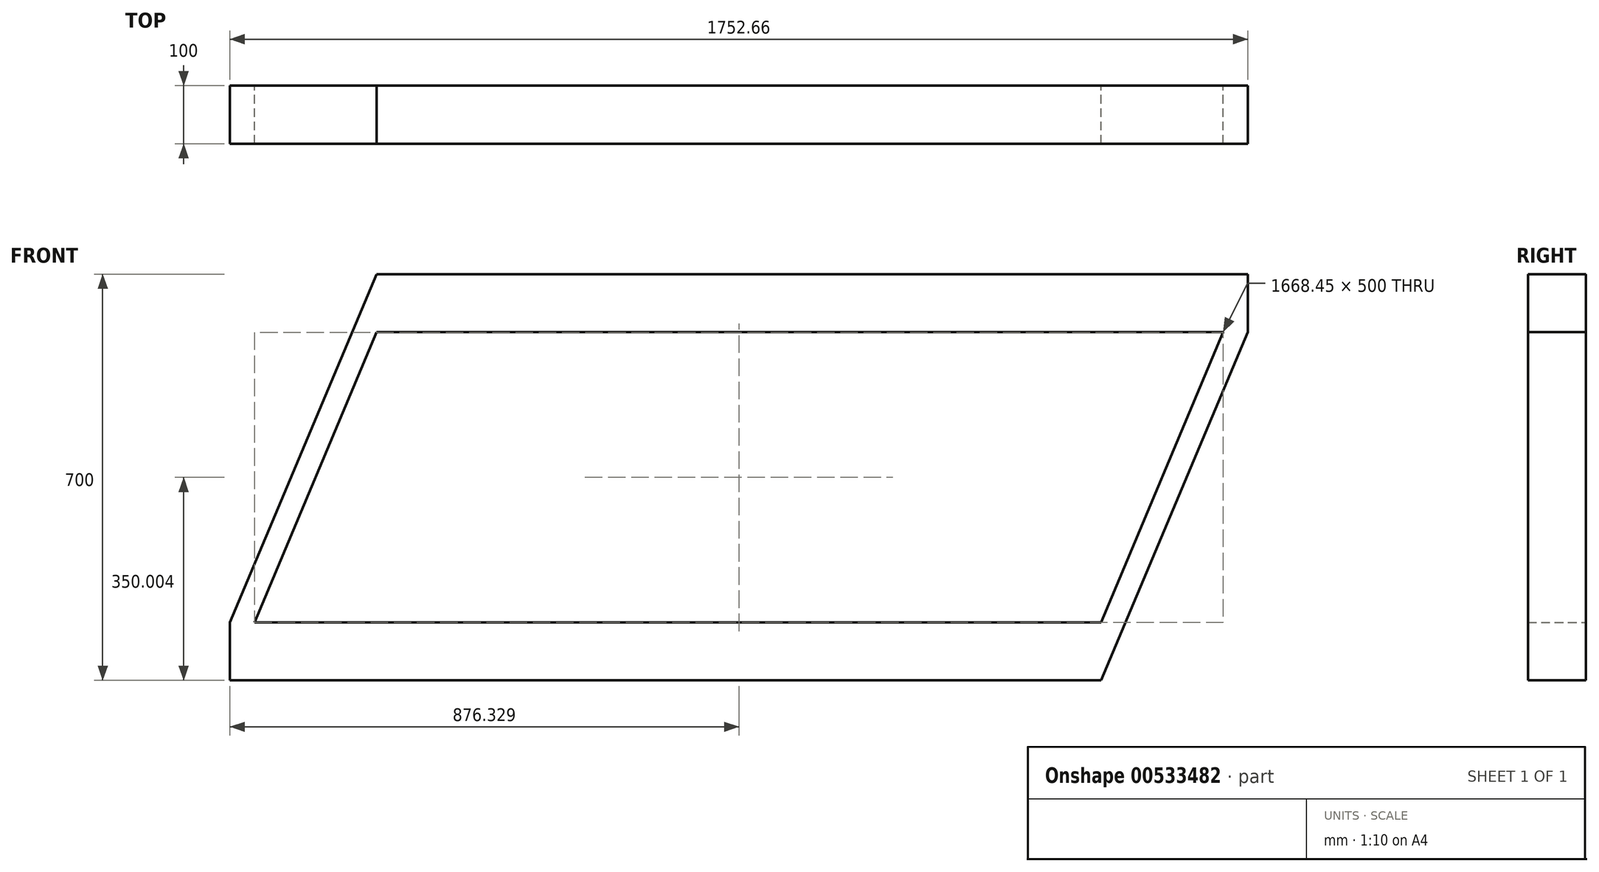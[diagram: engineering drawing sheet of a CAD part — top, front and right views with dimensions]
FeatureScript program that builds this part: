
annotation { "Feature Type Name" : "Feature", "Feature Type Description" : "" }
export const myFeature = defineFeature(function(context is Context, id is Id, definition is map)
    precondition{}
    {
        {
            var Q0;
            Q0=qCreatedBy(makeId("Front.planeOp"),FACE);
            var sketch = newSketch(context, id + "F0", { "sketchPlane" : qUnion([Q0])});
            skLineSegment(sketch, "E0.bottom", {"start": v(-429.7, -1038.94) * mm, "end": v(1070.3, -1038.94) * mm});
            skLineSegment(sketch, "E0.top", {"start": v(-429.7, -938.94) * mm, "end": v(1070.3, -938.94) * mm});
            skLineSegment(sketch, "E0.left", {"start": v(-429.7, -1038.94) * mm, "end": v(-429.7, -938.94) * mm});
            skLineSegment(sketch, "E0.right", {"start": v(1070.3, -1038.94) * mm, "end": v(1070.3, -938.94) * mm});
            skLineSegment(sketch, "E1", {"start": v(-429.7, -938.94) * mm, "end": v(-177.03, -338.94) * mm});
            skLineSegment(sketch, "E2.bottom", {"start": v(-177.03, -338.94) * mm, "end": v(1322.97, -338.94) * mm});
            skLineSegment(sketch, "E2.top", {"start": v(-177.03, -438.94) * mm, "end": v(1322.97, -438.94) * mm});
            skLineSegment(sketch, "E2.left", {"start": v(-177.03, -338.94) * mm, "end": v(-177.03, -438.94) * mm});
            skLineSegment(sketch, "E2.right", {"start": v(1322.97, -338.94) * mm, "end": v(1322.97, -438.94) * mm});
            skLineSegment(sketch, "E3", {"start": v(1322.97, -338.94) * mm, "end": v(1070.3, -938.94) * mm});
            skLineSegment(sketch, "E4", {"start": v(1322.97, -438.94) * mm, "end": v(1070.3, -1038.94) * mm});
            skLineSegment(sketch, "E5", {"start": v(-177.03, -438.94) * mm, "end": v(-429.7, -1038.94) * mm});
            skLineSegment(sketch, "E6", {"start": v(-345.47, -738.94) * mm, "end": v(1154.53, -738.94) * mm});
            skSolve(sketch);
        }
        {
            var Q0;
            {var subQ0=sQuery(id+"F0.wireOp",EDGE,"E2.bottom");Q0=makeQuery(id+"F0.imprint","IMPRINT",FACE,{"disambiguationData":[TD([[makeQuery(id+"F0.imprint","IMPRINT",EDGE,{"derivedFrom":subQ0}),-1.0]])]});}
            extrude(context, id + "F1", {"entities" : qUnion([Q0]), "depth" : 100 * mm, "offsetDistance" : 25 * mm});
        }
        {
            var Q0;
            {var subQ0=sQuery(id+"F0.wireOp",EDGE,"E2.left");Q0=makeQuery(id+"F0.imprint","IMPRINT",FACE,{"disambiguationData":[TD([[makeQuery(id+"F0.imprint","IMPRINT",EDGE,{"derivedFrom":subQ0}),-1.0]])]});}
            var Q1;
            {var subQ1=sQuery(id+"F0.wireOp",EDGE,"E0.top");var subQ3=sQuery(id+"F0.wireOp",EDGE,"E5");var subQ4=makeQuery(id+"F0.imprint","INTERSECT",VERTEX,{"derivedFrom":[subQ1,subQ3]});Q1=makeQuery(id+"F0.imprint","IMPRINT",FACE,{"disambiguationData":[TD([[makeQuery(id+"F0.imprint","IMPRINT",EDGE,{"disambiguationData":[TD([[subQ4,1.0]])],"derivedFrom":subQ3}),-1.0]])]});}
            var Q2;
            {var subQ0=sQuery(id+"F0.wireOp",EDGE,"E0.left");Q2=makeQuery(id+"F0.imprint","IMPRINT",FACE,{"disambiguationData":[TD([[makeQuery(id+"F0.imprint","IMPRINT",EDGE,{"derivedFrom":subQ0}),-1.0]])]});}
            extrude(context, id + "F2", {"entities" : qUnion([Q0, Q1, Q2]), "operationType" : NewBodyOperationType.ADD, "depth" : 100 * mm, "offsetDistance" : 25 * mm});
        }
        {
            var Q0;
            {var subQ0=sQuery(id+"F0.wireOp",EDGE,"E2.right");Q0=makeQuery(id+"F0.imprint","IMPRINT",FACE,{"disambiguationData":[TD([[makeQuery(id+"F0.imprint","IMPRINT",EDGE,{"derivedFrom":subQ0}),-1.0]])]});}
            var Q1;
            {var subQ4=sQuery(id+"F0.wireOp",EDGE,"E0.right");Q1=makeQuery(id+"F0.imprint","IMPRINT",FACE,{"disambiguationData":[TD([[makeQuery(id+"F0.imprint","IMPRINT",EDGE,{"derivedFrom":subQ4}),-1.0]])]});}
            var Q2;
            {var subQ0=sQuery(id+"F0.wireOp",EDGE,"E0.bottom");Q2=makeQuery(id+"F0.imprint","IMPRINT",FACE,{"disambiguationData":[TD([[makeQuery(id+"F0.imprint","IMPRINT",EDGE,{"derivedFrom":subQ0}),1.0]])]});}
            extrude(context, id + "F3", {"entities" : qUnion([Q0, Q1, Q2]), "operationType" : NewBodyOperationType.ADD, "depth" : 100 * mm, "offsetDistance" : 25 * mm});
        }
    });
